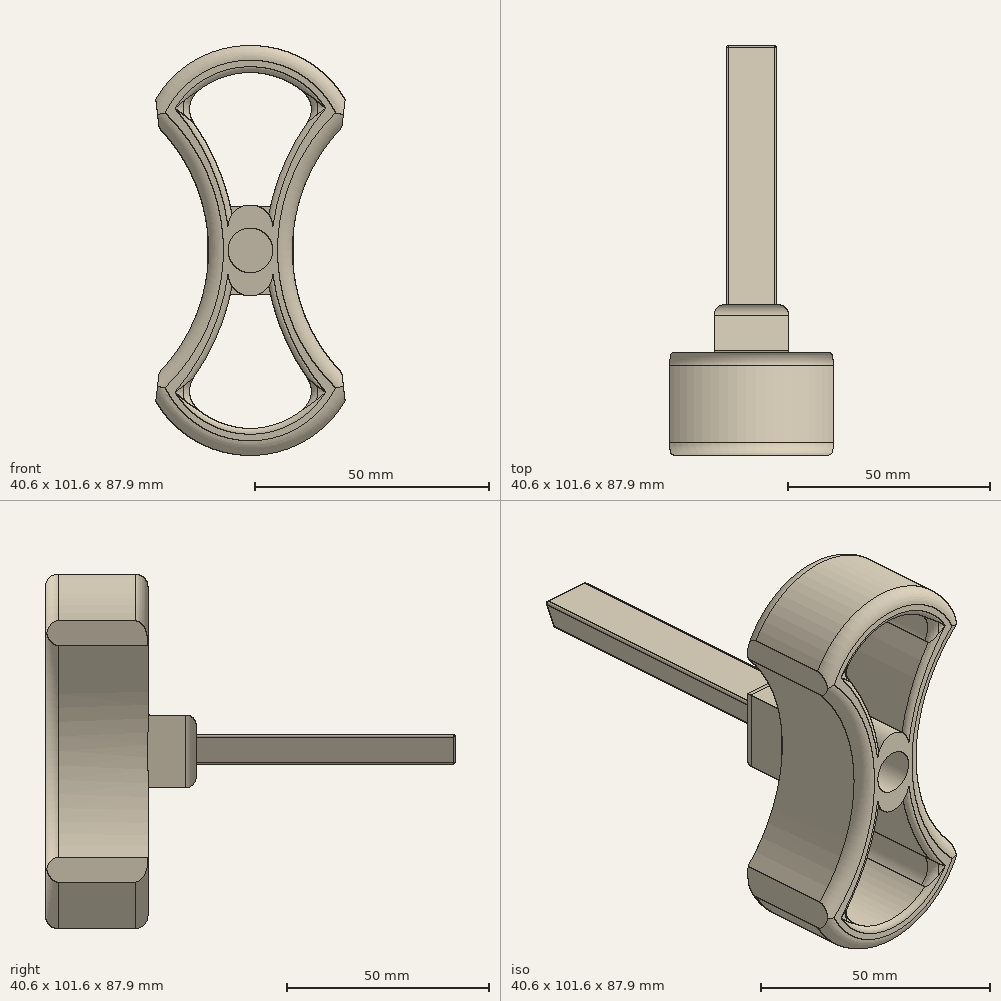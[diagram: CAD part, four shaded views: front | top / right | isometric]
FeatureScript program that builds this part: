
annotation { "Feature Type Name" : "Feature", "Feature Type Description" : "" }
export const myFeature = defineFeature(function(context is Context, id is Id, definition is map)
    precondition{}
    {
        {
            var Q0;
            Q0=qCreatedBy(makeId("Front.planeOp"),FACE);
            var sketch = newSketch(context, id + "F0", { "sketchPlane" : qUnion([Q0])});
            skPoint(sketch, "E0", {"position": v(-22.08, 28.63) * mm});
            skPoint(sketch, "E1.MirrorP", {"position": v(-22.08, -28.63) * mm});
            skArc(sketch, "E2", {"start": v(-22.08, -28.63) * mm, "mid": v(-8.97, 0) * mm, "end": v(-22.08, 28.63) * mm});
            skArc(sketch, "E3.MirrorCS", {"start": v(22.08, -28.63) * mm, "mid": v(8.97, 0) * mm, "end": v(22.08, 28.63) * mm});
            skArc(sketch, "E4", {"start": v(22.08, 28.63) * mm, "mid": v(0, 43.95) * mm, "end": v(-22.08, 28.63) * mm});
            skArc(sketch, "E5.MirrorCS", {"start": v(22.08, -28.63) * mm, "mid": v(0, -43.95) * mm, "end": v(-22.08, -28.63) * mm});
            skArc(sketch, "E6.0", {"start": v(14.9, 29.98) * mm, "mid": v(0.3, 38.1) * mm, "end": v(-14.57, 30.49) * mm});
            skArc(sketch, "E6.2", {"start": v(14.9, -29.98) * mm, "mid": v(0, -38.1) * mm, "end": v(-14.9, -29.98) * mm});
            skPoint(sketch, "E7", {"position": v(-3.92, 7.69) * mm});
            skPoint(sketch, "E8.MirrorP", {"position": v(-3.92, -7.69) * mm});
            skPoint(sketch, "E9.MirrorP", {"position": v(3.92, 7.69) * mm});
            skPoint(sketch, "E10.MirrorP", {"position": v(3.92, -7.69) * mm});
            skPoint(sketch, "E11", {"position": v(-0.01, 4.76) * mm});
            skPoint(sketch, "E12.MirrorP", {"position": v(-0.01, -4.76) * mm});
            skCircle(sketch, "E13", {"center": v(0, 0) * mm, "radius": 4.76 * mm});
            skArc(sketch, "E14", {"start": v(3.92, 7.69) * mm, "mid": v(0, 9.75) * mm, "end": v(-3.92, 7.69) * mm});
            skArc(sketch, "E15.MirrorCS", {"start": v(3.92, -7.69) * mm, "mid": v(0, -9.75) * mm, "end": v(-3.92, -7.69) * mm});
            skArc(sketch, "E16", {"start": v(-3.92, 7.69) * mm, "mid": v(-7.81, 19.76) * mm, "end": v(-14.57, 30.49) * mm});
            skArc(sketch, "E17.MirrorCS", {"start": v(-3.92, -7.69) * mm, "mid": v(-7.81, -19.76) * mm, "end": v(-14.57, -30.49) * mm});
            skArc(sketch, "E18.MirrorCS", {"start": v(3.92, 7.69) * mm, "mid": v(7.81, 19.76) * mm, "end": v(14.57, 30.49) * mm});
            skArc(sketch, "E19.MirrorCS", {"start": v(3.92, -7.69) * mm, "mid": v(7.81, -19.76) * mm, "end": v(14.57, -30.49) * mm});
            skSolve(sketch);
        }
        {
            var Q0;
            Q0=makeQuery(id+"F0.imprint","IMPRINT",FACE,{"disambiguationData":[TD([[makeQuery(id+"F0.imprint","IMPRINT",EDGE,{"derivedFrom":sQuery(id+"F0.wireOp",EDGE,"E2")}),-1.0]])]});
            extrude(context, id + "F1", {"entities" : qUnion([Q0]), "depth" : 25.4 * mm, "offsetDistance" : 25.4 * mm});
        }
        {
            var Q0;
            Q0=makeQuery(id+"F1.opExtrude","SWEPT_EDGE",EDGE,{"disambiguationData":[OSD([sQuery(id+"F0.wireOp",EDGE,"E2"),sQuery(id+"F0.wireOp",EDGE,"E4")])]});
            var Q1;
            Q1=makeQuery(id+"F1.opExtrude","SWEPT_EDGE",EDGE,{"disambiguationData":[OSD([sQuery(id+"F0.wireOp",EDGE,"E2"),sQuery(id+"F0.wireOp",EDGE,"E5.MirrorCS")])]});
            var Q2;
            Q2=makeQuery(id+"F1.opExtrude","SWEPT_EDGE",EDGE,{"disambiguationData":[OSD([sQuery(id+"F0.wireOp",EDGE,"E3.MirrorCS"),sQuery(id+"F0.wireOp",EDGE,"E4")])]});
            var Q3;
            Q3=makeQuery(id+"F1.opExtrude","SWEPT_EDGE",EDGE,{"disambiguationData":[OSD([sQuery(id+"F0.wireOp",EDGE,"E3.MirrorCS"),sQuery(id+"F0.wireOp",EDGE,"E5.MirrorCS")])]});
            chamfer(context, id + "F2", {"entities" : qUnion([Q0, Q1, Q2, Q3]), "width" : 5.08 * mm, "tangentPropagation" : true});
        }
        {
            var Q0;
            Q0=makeQuery(id+"F1.opExtrude","CAP_EDGE",EDGE,{"disambiguationData":[OSD([sQuery(id+"F0.wireOp",EDGE,"E19.MirrorCS")])],"isStart":false});
            var Q1;
            Q1=makeQuery(id+"F1.opExtrude","CAP_EDGE",EDGE,{"disambiguationData":[OSD([sQuery(id+"F0.wireOp",EDGE,"E17.MirrorCS")])],"isStart":false});
            var Q2;
            Q2=makeQuery(id+"F1.opExtrude","CAP_EDGE",EDGE,{"disambiguationData":[OSD([sQuery(id+"F0.wireOp",EDGE,"E6.2")])],"isStart":false});
            var Q3;
            Q3=makeQuery(id+"F1.opExtrude","CAP_EDGE",EDGE,{"disambiguationData":[OSD([sQuery(id+"F0.wireOp",EDGE,"E16")])],"isStart":false});
            var Q4;
            Q4=makeQuery(id+"F1.opExtrude","CAP_EDGE",EDGE,{"disambiguationData":[OSD([sQuery(id+"F0.wireOp",EDGE,"E18.MirrorCS")])],"isStart":false});
            var Q5;
            Q5=makeQuery(id+"F1.opExtrude","CAP_EDGE",EDGE,{"disambiguationData":[OSD([sQuery(id+"F0.wireOp",EDGE,"E6.0")])],"isStart":false});
            var Q6;
            Q6=makeQuery(id+"F1.opExtrude","CAP_EDGE",EDGE,{"disambiguationData":[OSD([sQuery(id+"F0.wireOp",EDGE,"E6.0")])],"isStart":true});
            var Q7;
            Q7=makeQuery(id+"F1.opExtrude","CAP_EDGE",EDGE,{"disambiguationData":[OSD([sQuery(id+"F0.wireOp",EDGE,"E18.MirrorCS")])],"isStart":true});
            var Q8;
            Q8=makeQuery(id+"F1.opExtrude","CAP_EDGE",EDGE,{"disambiguationData":[OSD([sQuery(id+"F0.wireOp",EDGE,"E16")])],"isStart":true});
            var Q9;
            Q9=makeQuery(id+"F1.opExtrude","CAP_EDGE",EDGE,{"disambiguationData":[OSD([sQuery(id+"F0.wireOp",EDGE,"E19.MirrorCS")])],"isStart":true});
            var Q10;
            Q10=makeQuery(id+"F1.opExtrude","CAP_EDGE",EDGE,{"disambiguationData":[OSD([sQuery(id+"F0.wireOp",EDGE,"E17.MirrorCS")])],"isStart":true});
            var Q11;
            Q11=makeQuery(id+"F1.opExtrude","CAP_EDGE",EDGE,{"disambiguationData":[OSD([sQuery(id+"F0.wireOp",EDGE,"E6.2")])],"isStart":true});
            fillet(context, id + "F3", {"entities" : qUnion([Q0, Q1, Q2, Q3, Q4, Q5, Q6, Q7, Q8, Q9, Q10, Q11]), "radius" : 1.27 * mm, "tangentPropagation" : true, "allowEdgeOverflow" : false});
        }
        {
            var Q0;
            Q0=makeQuery(id+"F1.opExtrude","CAP_EDGE",EDGE,{"disambiguationData":[OSD([sQuery(id+"F0.wireOp",EDGE,"E3.MirrorCS")])],"isStart":false});
            var Q1;
            Q1=makeQuery(id+"F1.opExtrude","CAP_EDGE",EDGE,{"disambiguationData":[OSD([sQuery(id+"F0.wireOp",EDGE,"E2")])],"isStart":false});
            var Q2;
            Q2=makeQuery(id+"F1.opExtrude","CAP_EDGE",EDGE,{"disambiguationData":[OSD([sQuery(id+"F0.wireOp",EDGE,"E4")])],"isStart":false});
            var Q3;
            Q3=makeQuery(id+"F1.opExtrude","CAP_EDGE",EDGE,{"disambiguationData":[OSD([sQuery(id+"F0.wireOp",EDGE,"E5.MirrorCS")])],"isStart":false});
            var Q4;
            Q4=makeQuery(id+"F1.opExtrude","CAP_EDGE",EDGE,{"disambiguationData":[OSD([sQuery(id+"F0.wireOp",EDGE,"E5.MirrorCS")])],"isStart":true});
            var Q5;
            Q5=makeQuery(id+"F1.opExtrude","CAP_EDGE",EDGE,{"disambiguationData":[OSD([sQuery(id+"F0.wireOp",EDGE,"E4")])],"isStart":true});
            fillet(context, id + "F4", {"entities" : qUnion([Q0, Q1, Q2, Q3, Q4, Q5]), "radius" : 3.17 * mm, "tangentPropagation" : true, "allowEdgeOverflow" : false});
        }
        {
            var Q0;
            Q0=qCreatedBy(makeId("Front.planeOp"),FACE);
            var sketch = newSketch(context, id + "F5", { "sketchPlane" : qUnion([Q0])});
            skLineSegment(sketch, "E20.bottom", {"start": v(-9.25, 9) * mm, "end": v(9.25, 9) * mm});
            skLineSegment(sketch, "E20.top", {"start": v(-9.25, -9) * mm, "end": v(9.25, -9) * mm});
            skLineSegment(sketch, "E20.left", {"start": v(-9.25, 9) * mm, "end": v(-9.25, -9) * mm});
            skLineSegment(sketch, "E20.right", {"start": v(9.25, 9) * mm, "end": v(9.25, -9) * mm});
            skPoint(sketch, "E20.middle", {"position": v(0, 0) * mm});
            skSolve(sketch);
        }
        {
            var Q0;
            Q0 = qSketchRegion(id + "F5", true);
            extrude(context, id + "F6", {"entities" : qUnion([Q0]), "operationType" : NewBodyOperationType.ADD, "oppositeDirection" : true, "depth" : 11.94 * mm, "offsetDistance" : 25.4 * mm});
        }
        {
            var Q0;
            Q0=qCreatedBy(makeId("Front.planeOp"),FACE);
            var sketch = newSketch(context, id + "F7", { "sketchPlane" : qUnion([Q0])});
            skLineSegment(sketch, "E21", {"start": v(0, 4.21) * mm, "end": v(-6.35, 4.21) * mm});
            skLineSegment(sketch, "E22.MirrorCS", {"start": v(0, 4.21) * mm, "end": v(6.35, 4.21) * mm});
            skLineSegment(sketch, "E23", {"start": v(0, -3.18) * mm, "end": v(-3.81, -3.18) * mm});
            skLineSegment(sketch, "E24.MirrorCS", {"start": v(0, -3.18) * mm, "end": v(3.81, -3.18) * mm});
            skLineSegment(sketch, "E25", {"start": v(6.35, 4.21) * mm, "end": v(3.8, -3.18) * mm});
            skLineSegment(sketch, "E26", {"start": v(-3.8, -3.18) * mm, "end": v(-6.35, 4.21) * mm});
            skLineSegment(sketch, "E27.0", {"start": v(0, 2.3) * mm, "end": v(3.68, 2.3) * mm});
            skLineSegment(sketch, "E27.1", {"start": v(0, -1.28) * mm, "end": v(2.45, -1.28) * mm});
            skLineSegment(sketch, "E27.2", {"start": v(0, -1.28) * mm, "end": v(-2.45, -1.28) * mm});
            skLineSegment(sketch, "E27.3", {"start": v(3.68, 2.3) * mm, "end": v(2.45, -1.28) * mm});
            skLineSegment(sketch, "E27.4", {"start": v(-2.45, -1.28) * mm, "end": v(-3.68, 2.3) * mm});
            skLineSegment(sketch, "E27.5", {"start": v(0, 2.3) * mm, "end": v(-3.68, 2.3) * mm});
            skSolve(sketch);
        }
        {
            var Q0;
            Q0 = qSketchRegion(id + "F7", true);
            extrude(context, id + "F8", {"entities" : qUnion([Q0]), "operationType" : NewBodyOperationType.ADD, "oppositeDirection" : true, "depth" : 76.2 * mm, "offsetDistance" : 25.4 * mm});
        }
        {
            var Q0;
            Q0=makeQuery(id+"F8.opExtrude","CAP_FACE",FACE,{"disambiguationData":[OSD([sQuery(id+"F7.wireOp",EDGE,"E21"),sQuery(id+"F7.wireOp",EDGE,"E22.MirrorCS"),sQuery(id+"F7.wireOp",EDGE,"E23"),sQuery(id+"F7.wireOp",EDGE,"E24.MirrorCS"),sQuery(id+"F7.wireOp",EDGE,"E25"),sQuery(id+"F7.wireOp",EDGE,"E26")])],"isStart":false});
            var Q1;
            Q1=makeQuery(id+"F8.opExtrude","SWEPT_EDGE",EDGE,{"disambiguationData":[OSD([sQuery(id+"F7.wireOp",EDGE,"E22.MirrorCS"),sQuery(id+"F7.wireOp",EDGE,"E25")])]});
            var Q2;
            Q2=makeQuery(id+"F8.opExtrude","SWEPT_EDGE",EDGE,{"disambiguationData":[OSD([sQuery(id+"F7.wireOp",EDGE,"E21"),sQuery(id+"F7.wireOp",EDGE,"E26")])]});
            var Q3;
            Q3=makeQuery(id+"F8.opExtrude","SWEPT_EDGE",EDGE,{"disambiguationData":[OSD([sQuery(id+"F7.wireOp",EDGE,"E24.MirrorCS"),sQuery(id+"F7.wireOp",EDGE,"E25")])]});
            var Q4;
            Q4=makeQuery(id+"F8.opExtrude","SWEPT_EDGE",EDGE,{"disambiguationData":[OSD([sQuery(id+"F7.wireOp",EDGE,"E23"),sQuery(id+"F7.wireOp",EDGE,"E26")])]});
            var Q5;
            {var subQ0=sQuery(id+"F5.wireOp",EDGE,"E20.left");var subQ1=sQuery(id+"F5.wireOp",EDGE,"E20.bottom");var subQ2=makeQuery(id+"F6.opExtrude","SWEPT_FACE",FACE,{"disambiguationData":[OSD([subQ1])]});var subQ3=sQuery(id+"F0.wireOp",EDGE,"E16");var subQ4=makeQuery(id+"F1.opExtrude","CAP_FACE",FACE,{"disambiguationData":[OSD([sQuery(id+"F0.wireOp",EDGE,"E2"),sQuery(id+"F0.wireOp",EDGE,"E3.MirrorCS"),sQuery(id+"F0.wireOp",EDGE,"E4"),sQuery(id+"F0.wireOp",EDGE,"E5.MirrorCS"),sQuery(id+"F0.wireOp",EDGE,"E6.0"),sQuery(id+"F0.wireOp",EDGE,"E6.2"),sQuery(id+"F0.wireOp",EDGE,"E13"),sQuery(id+"F0.wireOp",EDGE,"E14"),sQuery(id+"F0.wireOp",EDGE,"E15.MirrorCS"),subQ3,sQuery(id+"F0.wireOp",EDGE,"E17.MirrorCS"),sQuery(id+"F0.wireOp",EDGE,"E18.MirrorCS"),sQuery(id+"F0.wireOp",EDGE,"E19.MirrorCS")])],"isStart":true});Q5=makeQuery(id+"F6.boolean.opBoolean","SPLIT",EDGE,{"disambiguationData":[topologyDisambiguationEdgeConnected([subQ4,subQ2]),TD([makeQuery(id+"F6.opExtrude","SWEPT_FACE",FACE,{"disambiguationData":[OSD([subQ0])]})])],"derivedFrom":makeQuery(id+"F6.opExtrude","CAP_EDGE",EDGE,{"disambiguationData":[OSD([subQ1])],"isStart":true})});}
            var Q6;
            {var subQ0=sQuery(id+"F5.wireOp",EDGE,"E20.top");var subQ1=makeQuery(id+"F6.opExtrude","SWEPT_FACE",FACE,{"disambiguationData":[OSD([subQ0])]});var subQ2=sQuery(id+"F5.wireOp",EDGE,"E20.left");var subQ3=sQuery(id+"F0.wireOp",EDGE,"E17.MirrorCS");var subQ4=makeQuery(id+"F1.opExtrude","CAP_FACE",FACE,{"disambiguationData":[OSD([sQuery(id+"F0.wireOp",EDGE,"E2"),sQuery(id+"F0.wireOp",EDGE,"E3.MirrorCS"),sQuery(id+"F0.wireOp",EDGE,"E4"),sQuery(id+"F0.wireOp",EDGE,"E5.MirrorCS"),sQuery(id+"F0.wireOp",EDGE,"E6.0"),sQuery(id+"F0.wireOp",EDGE,"E6.2"),sQuery(id+"F0.wireOp",EDGE,"E13"),sQuery(id+"F0.wireOp",EDGE,"E14"),sQuery(id+"F0.wireOp",EDGE,"E15.MirrorCS"),sQuery(id+"F0.wireOp",EDGE,"E16"),subQ3,sQuery(id+"F0.wireOp",EDGE,"E18.MirrorCS"),sQuery(id+"F0.wireOp",EDGE,"E19.MirrorCS")])],"isStart":true});Q6=makeQuery(id+"F6.boolean.opBoolean","SPLIT",EDGE,{"disambiguationData":[topologyDisambiguationEdgeConnected([subQ4,subQ1]),TD([makeQuery(id+"F6.opExtrude","SWEPT_FACE",FACE,{"disambiguationData":[OSD([subQ2])]})])],"derivedFrom":makeQuery(id+"F6.opExtrude","CAP_EDGE",EDGE,{"disambiguationData":[OSD([subQ0])],"isStart":true})});}
            fillet(context, id + "F9", {"entities" : qUnion([Q0, Q1, Q2, Q3, Q4, Q5, Q6]), "radius" : 0.5 * mm, "tangentPropagation" : true, "allowEdgeOverflow" : false});
        }
        {
            var Q0;
            Q0=makeQuery(id+"F6.opExtrude","CAP_EDGE",EDGE,{"disambiguationData":[OSD([sQuery(id+"F5.wireOp",EDGE,"E20.left")])],"isStart":false});
            var Q1;
            Q1=makeQuery(id+"F6.opExtrude","CAP_EDGE",EDGE,{"disambiguationData":[OSD([sQuery(id+"F5.wireOp",EDGE,"E20.top")])],"isStart":false});
            var Q2;
            Q2=makeQuery(id+"F6.opExtrude","CAP_EDGE",EDGE,{"disambiguationData":[OSD([sQuery(id+"F5.wireOp",EDGE,"E20.right")])],"isStart":false});
            var Q3;
            Q3=makeQuery(id+"F6.opExtrude","CAP_EDGE",EDGE,{"disambiguationData":[OSD([sQuery(id+"F5.wireOp",EDGE,"E20.bottom")])],"isStart":false});
            fillet(context, id + "F10", {"entities" : qUnion([Q0, Q1, Q2, Q3]), "radius" : 2.54 * mm, "tangentPropagation" : true, "allowEdgeOverflow" : false});
        }
        {
            var Q0;
            Q0=makeQuery(id+"F1.opExtrude","SWEPT_EDGE",EDGE,{"disambiguationData":[OSD([sQuery(id+"F0.wireOp",EDGE,"E6.0"),sQuery(id+"F0.wireOp",EDGE,"E16")])]});
            var Q1;
            Q1=makeQuery(id+"F1.opExtrude","SWEPT_EDGE",EDGE,{"disambiguationData":[OSD([sQuery(id+"F0.wireOp",EDGE,"E6.2"),sQuery(id+"F0.wireOp",EDGE,"E17.MirrorCS")])]});
            var Q2;
            Q2=makeQuery(id+"F1.opExtrude","SWEPT_EDGE",EDGE,{"disambiguationData":[OSD([sQuery(id+"F0.wireOp",EDGE,"E6.0"),sQuery(id+"F0.wireOp",EDGE,"E18.MirrorCS")])]});
            var Q3;
            Q3=makeQuery(id+"F1.opExtrude","SWEPT_EDGE",EDGE,{"disambiguationData":[OSD([sQuery(id+"F0.wireOp",EDGE,"E6.2"),sQuery(id+"F0.wireOp",EDGE,"E19.MirrorCS")])]});
            fillet(context, id + "F11", {"entities" : qUnion([Q0, Q1, Q2, Q3]), "radius" : 5.08 * mm, "tangentPropagation" : true, "allowEdgeOverflow" : false});
        }
    });
